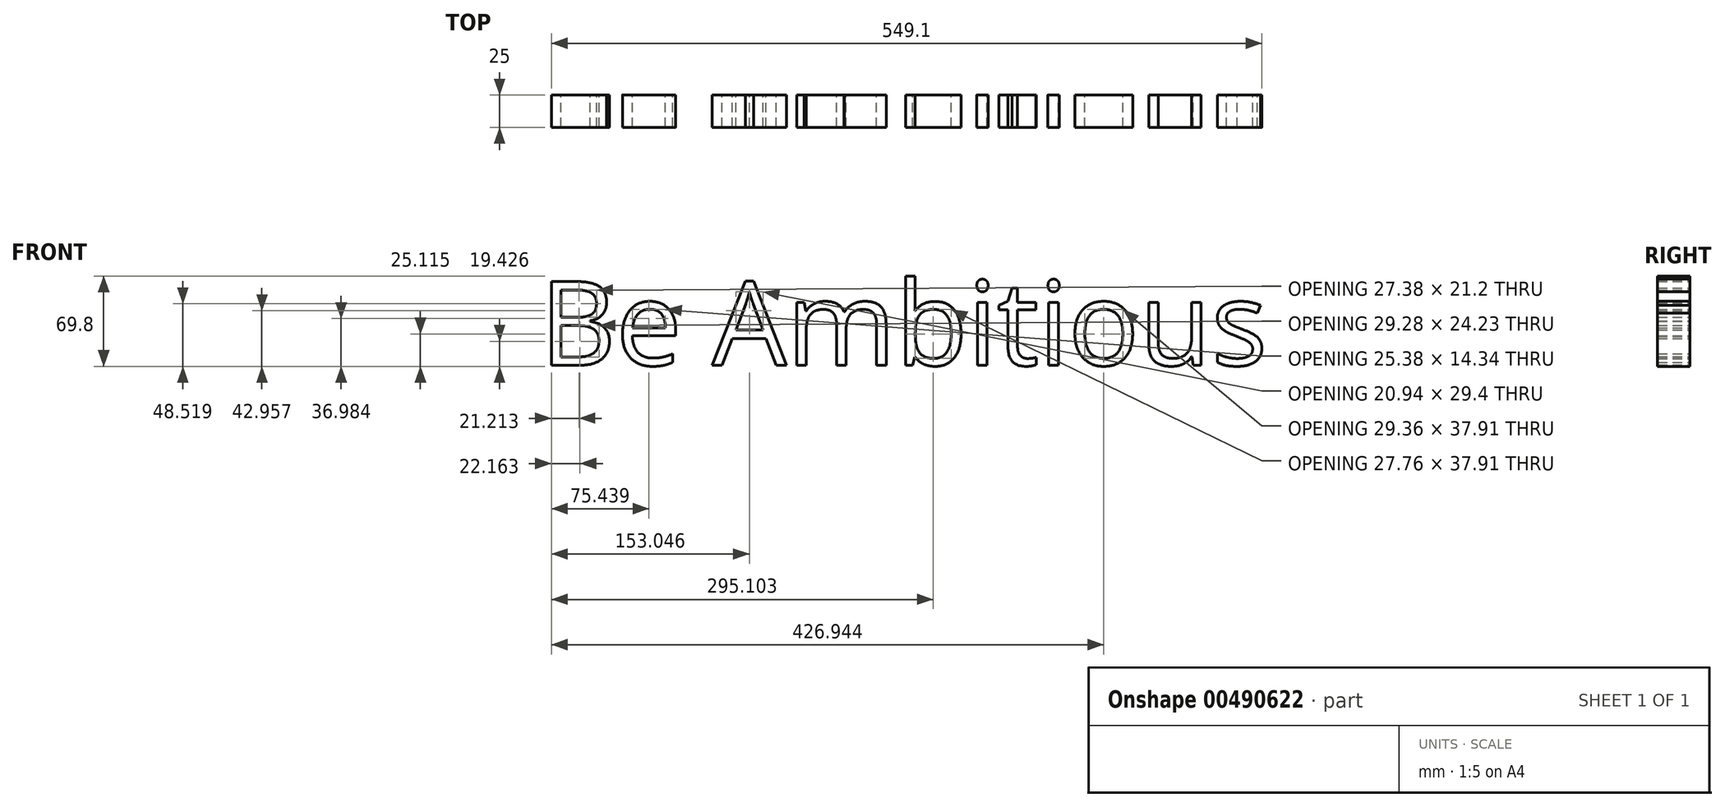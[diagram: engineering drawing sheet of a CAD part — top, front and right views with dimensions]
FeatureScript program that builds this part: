
annotation { "Feature Type Name" : "Feature", "Feature Type Description" : "" }
export const myFeature = defineFeature(function(context is Context, id is Id, definition is map)
    precondition{}
    {
        {
            var Q0;
            Q0=qCreatedBy(makeId("Front.planeOp"),FACE);
            var sketch = newSketch(context, id + "F0", { "sketchPlane" : qUnion([Q0])});
            skText(sketch, "E0", { "text": "Be Ambitious\n", "fontName": "OpenSans-Regular.ttf"});
            const initialGuessF0  = {"E0": [0, 0, 1, 0, 0.0653]};
            skSetInitialGuess(sketch, initialGuessF0);
            skSolve(sketch);
        }
        {
            var Q0;
            Q0 = qSketchRegion(id + "F0", true);
            extrude(context, id + "F1", {"entities" : qUnion([Q0]), "depth" : 25 * mm});
        }
    });
